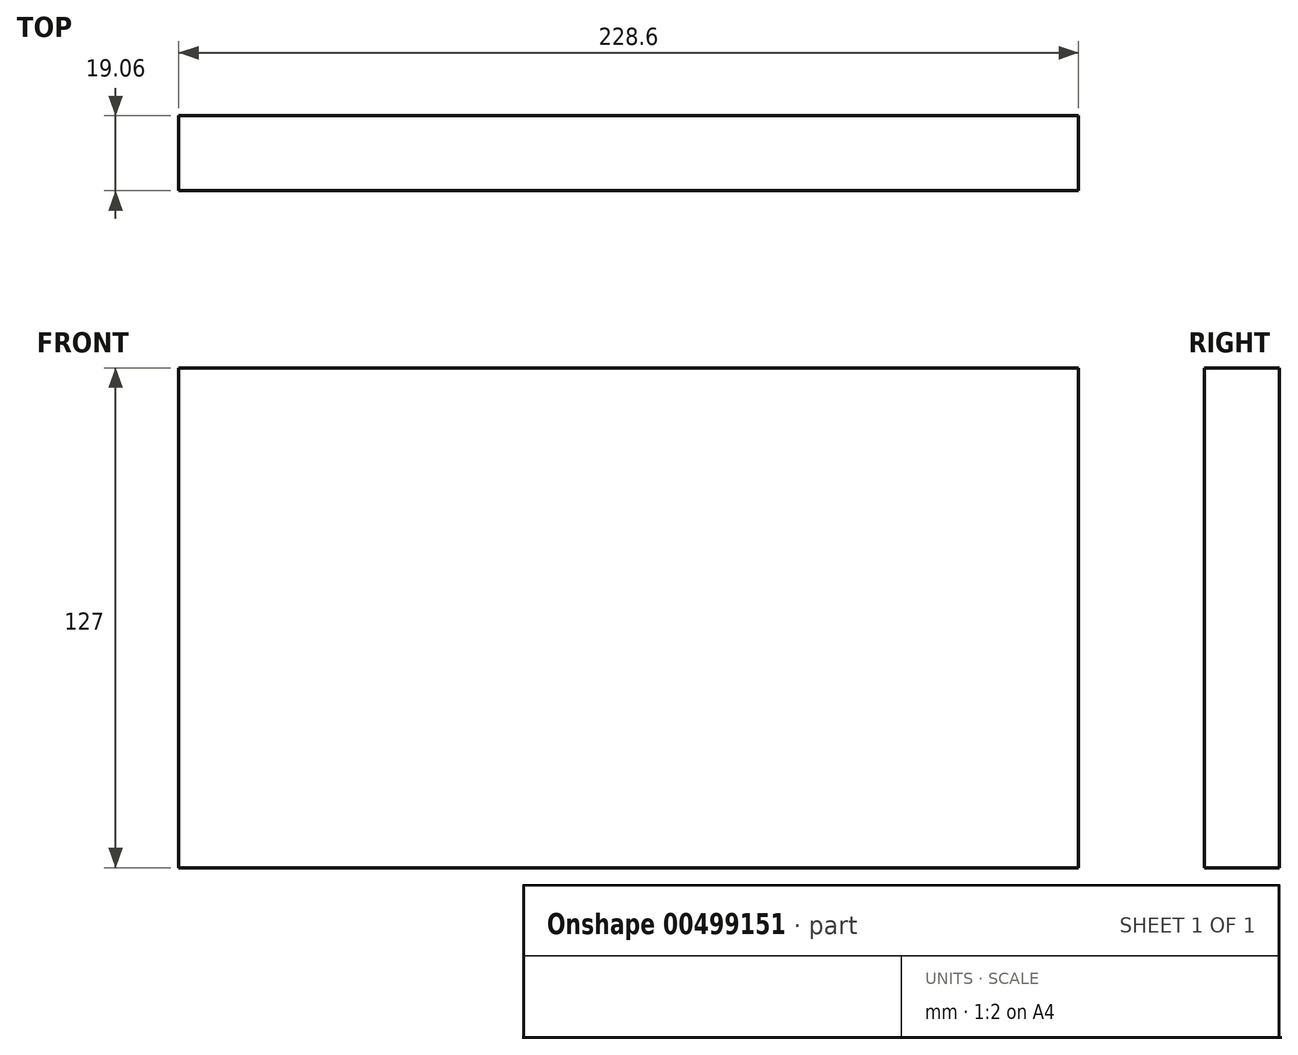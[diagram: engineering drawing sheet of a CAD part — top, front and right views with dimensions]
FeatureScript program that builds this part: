
annotation { "Feature Type Name" : "Feature", "Feature Type Description" : "" }
export const myFeature = defineFeature(function(context is Context, id is Id, definition is map)
    precondition{}
    {
        {
            var Q0;
            Q0=qCreatedBy(makeId("Top.planeOp"),FACE);
            var sketch = newSketch(context, id + "F0", { "sketchPlane" : qUnion([Q0])});
            skLineSegment(sketch, "E0.bottom", {"start": v(-114.3, 9.52) * mm, "end": v(114.3, 9.52) * mm});
            skLineSegment(sketch, "E0.top", {"start": v(-114.3, -9.52) * mm, "end": v(114.3, -9.52) * mm});
            skLineSegment(sketch, "E0.left", {"start": v(-114.3, 9.52) * mm, "end": v(-114.3, -9.53) * mm});
            skLineSegment(sketch, "E0.right", {"start": v(114.3, 9.52) * mm, "end": v(114.3, -9.53) * mm});
            skPoint(sketch, "E0.middle", {"position": v(0, 0) * mm});
            skSolve(sketch);
        }
        {
            var Q0;
            Q0=makeQuery(id+"F0.imprint","IMPRINT",FACE,{"disambiguationData":[TD([[makeQuery(id+"F0.imprint","IMPRINT",EDGE,{"derivedFrom":sQuery(id+"F0.wireOp",EDGE,"E0.bottom")}),-1.0]])]});
            extrude(context, id + "F1", {"entities" : qUnion([Q0]), "depth" : 127 * mm});
        }
    });
